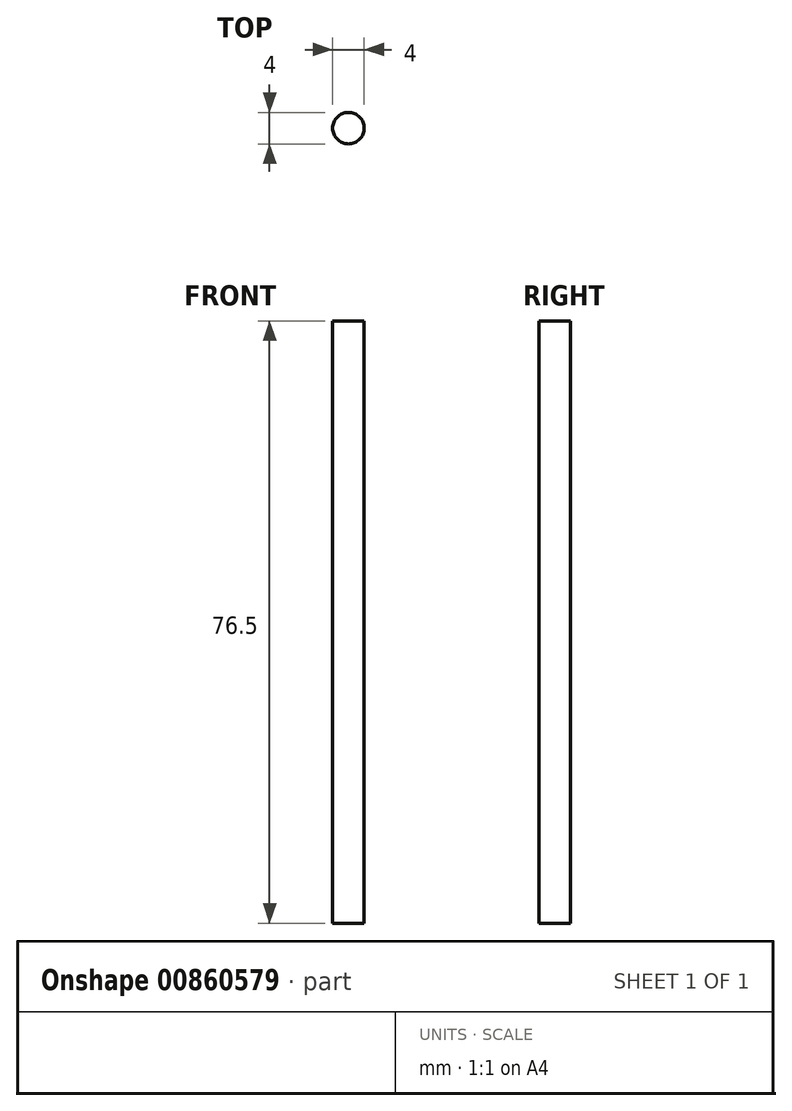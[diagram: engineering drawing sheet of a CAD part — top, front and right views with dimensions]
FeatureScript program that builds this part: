
annotation { "Feature Type Name" : "Feature", "Feature Type Description" : "" }
export const myFeature = defineFeature(function(context is Context, id is Id, definition is map)
    precondition{}
    {
        {
            var Q0;
            Q0=qCreatedBy(makeId("Top.planeOp"),FACE);
            var sketch = newSketch(context, id + "F0", { "sketchPlane" : qUnion([Q0])});
            skCircle(sketch, "E0", {"center": v(0, 0) * mm, "radius": 2 * mm});
            skSolve(sketch);
        }
        {
            var Q0;
            Q0 = qSketchRegion(id + "F0", true);
            extrude(context, id + "F1", {"entities" : qUnion([Q0]), "depth" : 76.5 * mm, "offsetDistance" : 25 * mm});
        }
    });
